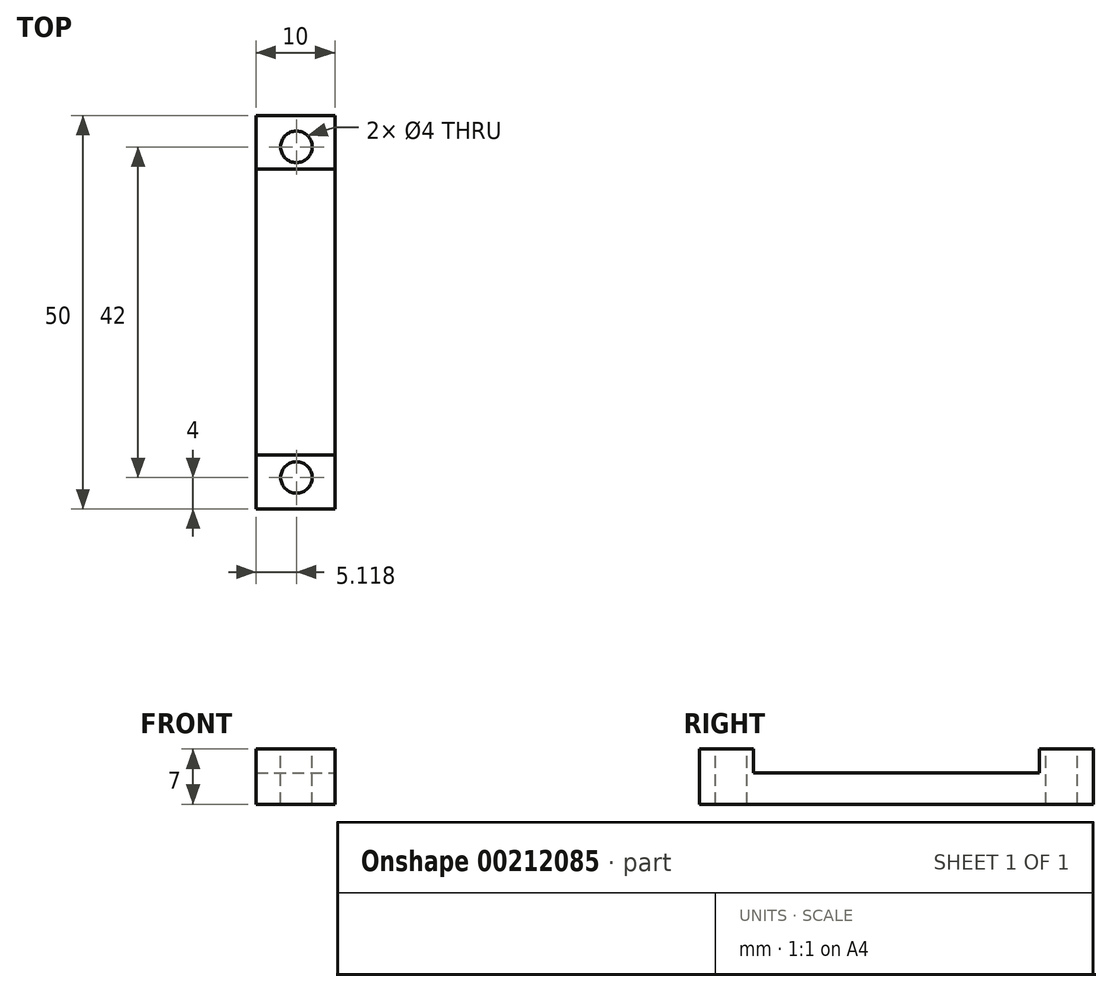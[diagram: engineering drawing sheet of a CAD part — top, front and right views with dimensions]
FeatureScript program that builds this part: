
annotation { "Feature Type Name" : "Feature", "Feature Type Description" : "" }
export const myFeature = defineFeature(function(context is Context, id is Id, definition is map)
    precondition{}
    {
        {
            var Q0;
            Q0=qCreatedBy(makeId("Top.planeOp"),FACE);
            var sketch = newSketch(context, id + "F0", { "sketchPlane" : qUnion([Q0])});
            skLineSegment(sketch, "E0.bottom", {"start": v(-10.23, 25) * mm, "end": v(-20.23, 25) * mm});
            skLineSegment(sketch, "E0.top", {"start": v(-10.23, -25) * mm, "end": v(-20.23, -25) * mm});
            skLineSegment(sketch, "E0.left", {"start": v(-10.23, 25) * mm, "end": v(-10.23, -25) * mm});
            skLineSegment(sketch, "E0.right", {"start": v(-20.23, 25) * mm, "end": v(-20.23, -25) * mm});
            skSolve(sketch);
        }
        {
            var Q0;
            Q0=makeQuery(id+"F0.imprint","IMPRINT",FACE,{"disambiguationData":[TD([[makeQuery(id+"F0.imprint","IMPRINT",EDGE,{"derivedFrom":sQuery(id+"F0.wireOp",EDGE,"E0.bottom")}),1.0]])]});
            extrude(context, id + "F1", {"entities" : qUnion([Q0]), "depth" : 4 * mm});
        }
        {
            var Q0;
            Q0=makeQuery(id+"F1.opExtrude","CAP_FACE",FACE,{"disambiguationData":[OSD([sQuery(id+"F0.wireOp",EDGE,"E0.bottom"),sQuery(id+"F0.wireOp",EDGE,"E0.top"),sQuery(id+"F0.wireOp",EDGE,"E0.left"),sQuery(id+"F0.wireOp",EDGE,"E0.right")])],"isStart":false});
            var sketch = newSketch(context, id + "F2", { "sketchPlane" : qUnion([Q0])});
            skLineSegment(sketch, "E1.bottom", {"start": v(-20.23, 25) * mm, "end": v(-10.23, 25) * mm});
            skLineSegment(sketch, "E1.top", {"start": v(-20.23, 18.17) * mm, "end": v(-10.23, 18.17) * mm});
            skLineSegment(sketch, "E1.left", {"start": v(-20.23, 25) * mm, "end": v(-20.23, 18.17) * mm});
            skLineSegment(sketch, "E1.right", {"start": v(-10.23, 25) * mm, "end": v(-10.23, 18.17) * mm});
            skLineSegment(sketch, "E2.MirrorCS", {"start": v(-20.23, -25) * mm, "end": v(-10.23, -25) * mm});
            skLineSegment(sketch, "E3.MirrorCS", {"start": v(-20.23, -18.17) * mm, "end": v(-10.23, -18.17) * mm});
            skLineSegment(sketch, "E4.MirrorCS", {"start": v(-20.23, -25) * mm, "end": v(-20.23, -18.17) * mm});
            skLineSegment(sketch, "E5.MirrorCS", {"start": v(-10.23, -25) * mm, "end": v(-10.23, -18.17) * mm});
            skSolve(sketch);
        }
        {
            var Q0;
            Q0=makeQuery(id+"F2.imprint","IMPRINT",FACE,{"disambiguationData":[TD([[makeQuery(id+"F2.imprint","IMPRINT",EDGE,{"derivedFrom":sQuery(id+"F2.wireOp",EDGE,"E1.bottom")}),1.0]])]});
            var Q1;
            Q1=makeQuery(id+"F2.imprint","IMPRINT",FACE,{"disambiguationData":[TD([[makeQuery(id+"F2.imprint","IMPRINT",EDGE,{"derivedFrom":sQuery(id+"F2.wireOp",EDGE,"E2.MirrorCS")}),-1.0]])]});
            extrude(context, id + "F3", {"entities" : qUnion([Q0, Q1]), "operationType" : NewBodyOperationType.ADD, "depth" : 3 * mm});
        }
        {
            var Q0;
            Q0=makeQuery(id+"F1.opExtrude","CAP_FACE",FACE,{"disambiguationData":[OSD([sQuery(id+"F0.wireOp",EDGE,"E0.bottom"),sQuery(id+"F0.wireOp",EDGE,"E0.top"),sQuery(id+"F0.wireOp",EDGE,"E0.left"),sQuery(id+"F0.wireOp",EDGE,"E0.right")])],"isStart":true});
            var sketch = newSketch(context, id + "F4", { "sketchPlane" : qUnion([Q0])});
            skLineSegment(sketch, "E6", {"start": v(-15.11, 21) * mm, "end": v(-15.11, -21) * mm});
            skSolve(sketch);
        }
        {
            var Q0;
            Q0=sQuery(id+"F4.wireOp",VERTEX,"E6.start");
            var Q1;
            Q1=sQuery(id+"F4.wireOp",VERTEX,"E6.end");
            var Q2;
            Q2=makeQuery(id+"F1.opExtrude","SWEPT_BODY",BODY,{"disambiguationData":[OSD([sQuery(id+"F0.wireOp",EDGE,"E0.bottom"),sQuery(id+"F0.wireOp",EDGE,"E0.top"),sQuery(id+"F0.wireOp",EDGE,"E0.left"),sQuery(id+"F0.wireOp",EDGE,"E0.right")])]});
            hole(context, id + "F5", {"style" : HoleStyle.SIMPLE, "endStyle" : HoleEndStyle.THROUGH, "holeDiameter" : 4 * mm, "locations" : qUnion([Q0, Q1]), "scope" : qUnion([Q2]), "isTappedThrough" : true});
        }
    });
